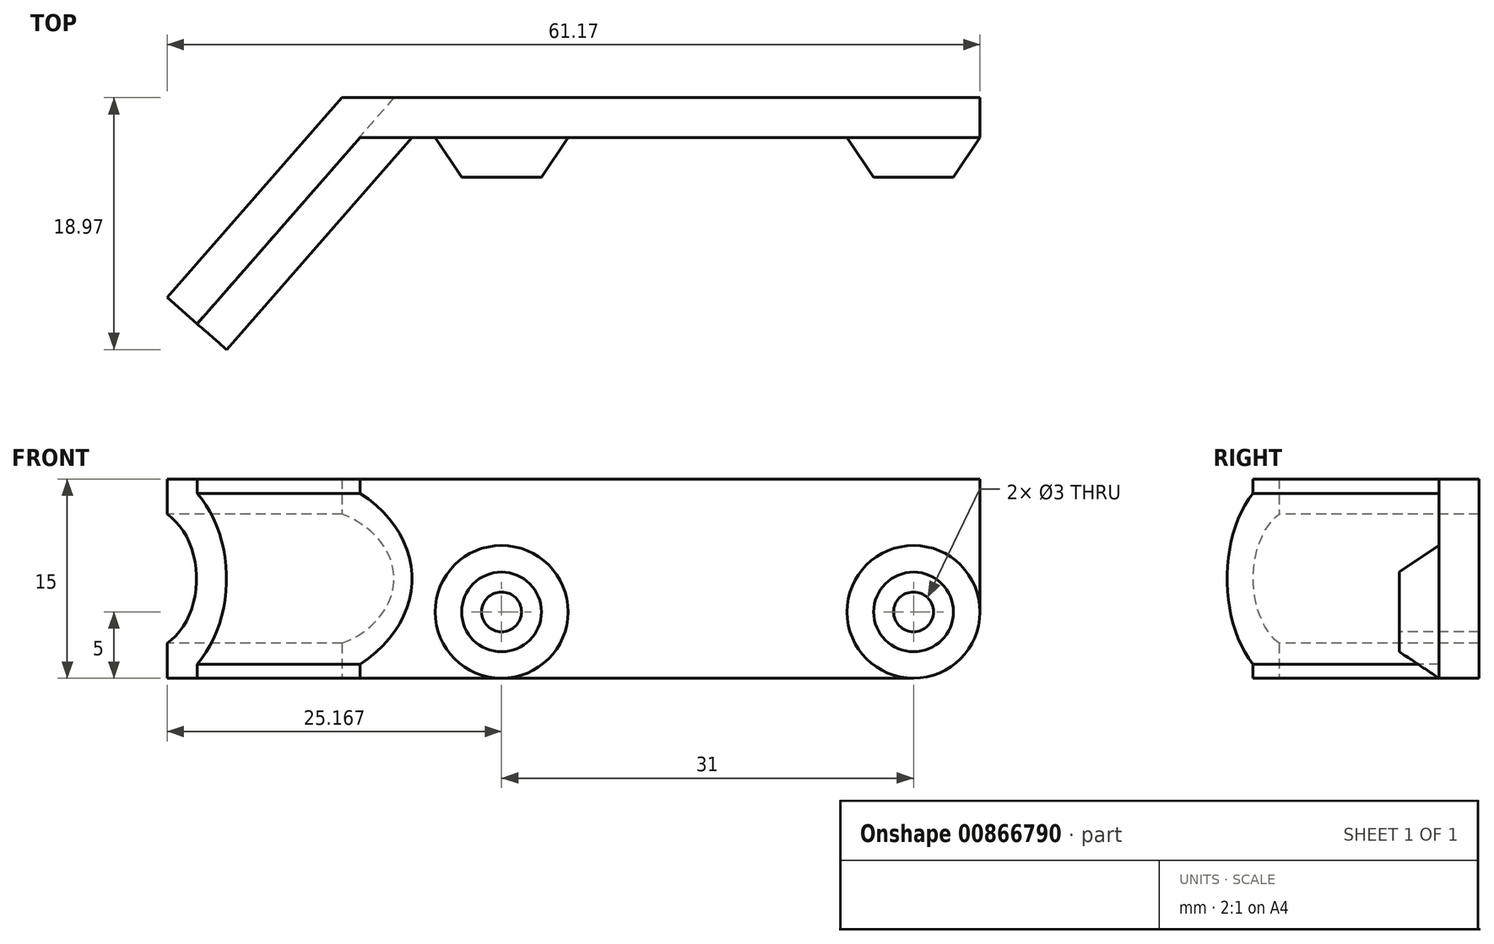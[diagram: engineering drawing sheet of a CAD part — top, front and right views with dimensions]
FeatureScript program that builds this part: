
annotation { "Feature Type Name" : "Feature", "Feature Type Description" : "" }
export const myFeature = defineFeature(function(context is Context, id is Id, definition is map)
    precondition{}
    {
        {
            var Q0;
            Q0=qCreatedBy(makeId("Top.planeOp"),FACE);
            var sketch = newSketch(context, id + "F0", { "sketchPlane" : qUnion([Q0])});
            skLineSegment(sketch, "E0", {"start": v(41.89, 0) * mm, "end": v(41.89, 3) * mm});
            skLineSegment(sketch, "E1", {"start": v(41.89, 3) * mm, "end": v(-6.11, 3) * mm});
            skLineSegment(sketch, "E2", {"start": v(-6.11, 3) * mm, "end": v(-19.28, -12.05) * mm});
            skLineSegment(sketch, "E3", {"start": v(-19.28, -12.05) * mm, "end": v(-17.02, -14.03) * mm});
            skLineSegment(sketch, "E4", {"start": v(-17.02, -14.03) * mm, "end": v(-4.75, 0) * mm});
            skLineSegment(sketch, "E5", {"start": v(-4.75, 0) * mm, "end": v(41.89, 0) * mm});
            skSolve(sketch);
        }
        {
            var Q0;
            Q0=makeQuery(id+"F0.imprint","IMPRINT",FACE,{"disambiguationData":[TD([[makeQuery(id+"F0.imprint","IMPRINT",EDGE,{"derivedFrom":sQuery(id+"F0.wireOp",EDGE,"E0")}),1.0]])]});
            extrude(context, id + "F1", {"entities" : qUnion([Q0]), "depth" : 15 * mm, "offsetDistance" : 25 * mm});
        }
        {
            var Q0;
            Q0=makeQuery(id+"F1.opExtrude","SWEPT_FACE",FACE,{"disambiguationData":[OSD([sQuery(id+"F0.wireOp",EDGE,"E3")])]});
            var sketch = newSketch(context, id + "F2", { "sketchPlane" : qUnion([Q0])});
            skCircle(sketch, "E6", {"center": v(-9.13, 7.5) * mm, "radius": 5.5 * mm});
            skPoint(sketch, "E6.centerSnap0", {"position": v(-6.58, 7.5) * mm});
            skCircle(sketch, "E7", {"center": v(-9.13, 7.5) * mm, "radius": 8.5 * mm});
            skLineSegment(sketch, "E8", {"start": v(-6.58, -0.6) * mm, "end": v(-6.58, 15.6) * mm});
            skSolve(sketch);
        }
        {
            var Q0;
            {var subQ0=sQuery(id+"F2.wireOp",EDGE,"E7");var subQ1=makeQuery(id+"F1.opExtrude","SWEPT_EDGE",EDGE,{"disambiguationData":[OSD([sQuery(id+"F0.wireOp",EDGE,"E3"),sQuery(id+"F0.wireOp",EDGE,"E4")])]});var subQ2=makeQuery(id+"F2.imprint","INTERSECT",VERTEX,{"disambiguationData":[OD(0.0)],"derivedFrom":[subQ1,subQ0]});Q0=makeQuery(id+"F2.imprint","IMPRINT",FACE,{"disambiguationData":[TD([[makeQuery(id+"F2.imprint","IMPRINT",EDGE,{"disambiguationData":[TD([[subQ2,1.0]])],"derivedFrom":subQ0}),1.0]])]});}
            extrude(context, id + "F3", {"entities" : qUnion([Q0]), "operationType" : NewBodyOperationType.ADD, "oppositeDirection" : true, "depth" : 22 * mm, "offsetDistance" : 25 * mm});
        }
        {
            var Q0;
            {var subQ0=sQuery(id+"F2.wireOp",EDGE,"E8");var subQ1=sQuery(id+"F2.wireOp",EDGE,"E6");var subQ2=makeQuery(id+"F2.imprint","INTERSECT",VERTEX,{"disambiguationData":[OD(0.0)],"derivedFrom":[subQ1,subQ0]});Q0=makeQuery(id+"F2.imprint","IMPRINT",FACE,{"disambiguationData":[TD([[makeQuery(id+"F2.imprint","IMPRINT",EDGE,{"disambiguationData":[TD([[subQ2,-1.0]])],"derivedFrom":subQ0}),1.0]])]});}
            extrude(context, id + "F4", {"entities" : qUnion([Q0]), "operationType" : NewBodyOperationType.REMOVE, "oppositeDirection" : true, "depth" : 25 * mm, "offsetDistance" : 25 * mm});
        }
        {
            var Q0;
            Q0=makeQuery(id+"F1.opExtrude","SWEPT_FACE",FACE,{"disambiguationData":[OSD([sQuery(id+"F0.wireOp",EDGE,"E5")])]});
            var sketch = newSketch(context, id + "F5", { "sketchPlane" : qUnion([Q0])});
            skPoint(sketch, "E9", {"position": v(36.89, 5) * mm});
            skPoint(sketch, "E10", {"position": v(5.89, 5) * mm});
            skCircle(sketch, "E11", {"center": v(5.89, 5) * mm, "radius": 5 * mm});
            skCircle(sketch, "E12", {"center": v(36.89, 5) * mm, "radius": 5 * mm});
            skSolve(sketch);
        }
        {
            var Q0;
            Q0=sQuery(id+"F5.wireOp",VERTEX,"E10");
            var Q1;
            Q1=sQuery(id+"F5.wireOp",VERTEX,"E9");
            var Q2;
            Q2=makeQuery(id+"F1.opExtrude","SWEPT_BODY",BODY,{"disambiguationData":[OSD([sQuery(id+"F0.wireOp",EDGE,"E0"),sQuery(id+"F0.wireOp",EDGE,"E1"),sQuery(id+"F0.wireOp",EDGE,"E2"),sQuery(id+"F0.wireOp",EDGE,"E3"),sQuery(id+"F0.wireOp",EDGE,"E4"),sQuery(id+"F0.wireOp",EDGE,"E5")])]});
            hole(context, id + "F6", {"style" : HoleStyle.SIMPLE, "endStyle" : HoleEndStyle.BLIND, "holeDiameter" : 3 * mm, "majorDiameter" : 5 * mm, "holeDepth" : 5 * mm, "isTappedThrough" : true, "tappedDepth" : 12 * mm, "tapClearance" : 3, "locations" : qUnion([Q0, Q1]), "scope" : qUnion([Q2])});
        }
        {
            var Q0;
            Q0=makeQuery(id+"F5.imprint","IMPRINT",FACE,{"disambiguationData":[TD([[makeQuery(id+"F5.imprint","IMPRINT",EDGE,{"derivedFrom":sQuery(id+"F5.wireOp",EDGE,"E11")}),1.0]])]});
            var Q1;
            Q1=makeQuery(id+"F5.imprint","IMPRINT",FACE,{"disambiguationData":[TD([[makeQuery(id+"F5.imprint","IMPRINT",EDGE,{"derivedFrom":sQuery(id+"F5.wireOp",EDGE,"E12")}),1.0]])]});
            extrude(context, id + "F7", {"entities" : qUnion([Q0, Q1]), "operationType" : NewBodyOperationType.ADD, "depth" : 3 * mm, "offsetDistance" : 25 * mm});
        }
        {
            var Q0;
            Q0=sQuery(id+"F5.wireOp",VERTEX,"E11.center");
            var Q1;
            Q1=sQuery(id+"F5.wireOp",VERTEX,"E9");
            var Q2;
            Q2=makeQuery(id+"F1.opExtrude","SWEPT_BODY",BODY,{"disambiguationData":[OSD([sQuery(id+"F0.wireOp",EDGE,"E0"),sQuery(id+"F0.wireOp",EDGE,"E1"),sQuery(id+"F0.wireOp",EDGE,"E2"),sQuery(id+"F0.wireOp",EDGE,"E3"),sQuery(id+"F0.wireOp",EDGE,"E4"),sQuery(id+"F0.wireOp",EDGE,"E5")])]});
            hole(context, id + "F8", {"style" : HoleStyle.SIMPLE, "endStyle" : HoleEndStyle.BLIND, "oppositeDirection" : true, "holeDiameter" : 3 * mm, "majorDiameter" : 5 * mm, "holeDepth" : 5 * mm, "isTappedThrough" : true, "tappedDepth" : 12 * mm, "tapClearance" : 3, "locations" : qUnion([Q0, Q1]), "scope" : qUnion([Q2])});
        }
        {
            var Q0;
            Q0=makeQuery(id+"F7.opExtrude","CAP_EDGE",EDGE,{"disambiguationData":[OSD([sQuery(id+"F5.wireOp",EDGE,"E11")])],"isStart":false});
            var Q1;
            Q1=makeQuery(id+"F7.opExtrude","CAP_EDGE",EDGE,{"disambiguationData":[OSD([sQuery(id+"F5.wireOp",EDGE,"E12")])],"isStart":false});
            chamfer(context, id + "F9", {"entities" : qUnion([Q0, Q1]), "chamferType" : ChamferType.TWO_OFFSETS, "width1" : 2 * mm, "oppositeDirection" : false, "width2" : 3 * mm, "tangentPropagation" : true});
        }
        {
            var Q0;
            Q0=makeQuery(id+"F1.opExtrude","CAP_EDGE",EDGE,{"disambiguationData":[OSD([sQuery(id+"F0.wireOp",EDGE,"E0")])],"isStart":true});
            fillet(context, id + "F10", {"entities" : qUnion([Q0]), "radius" : 5 * mm, "tangentPropagation" : true, "allowEdgeOverflow" : false});
        }
    });
